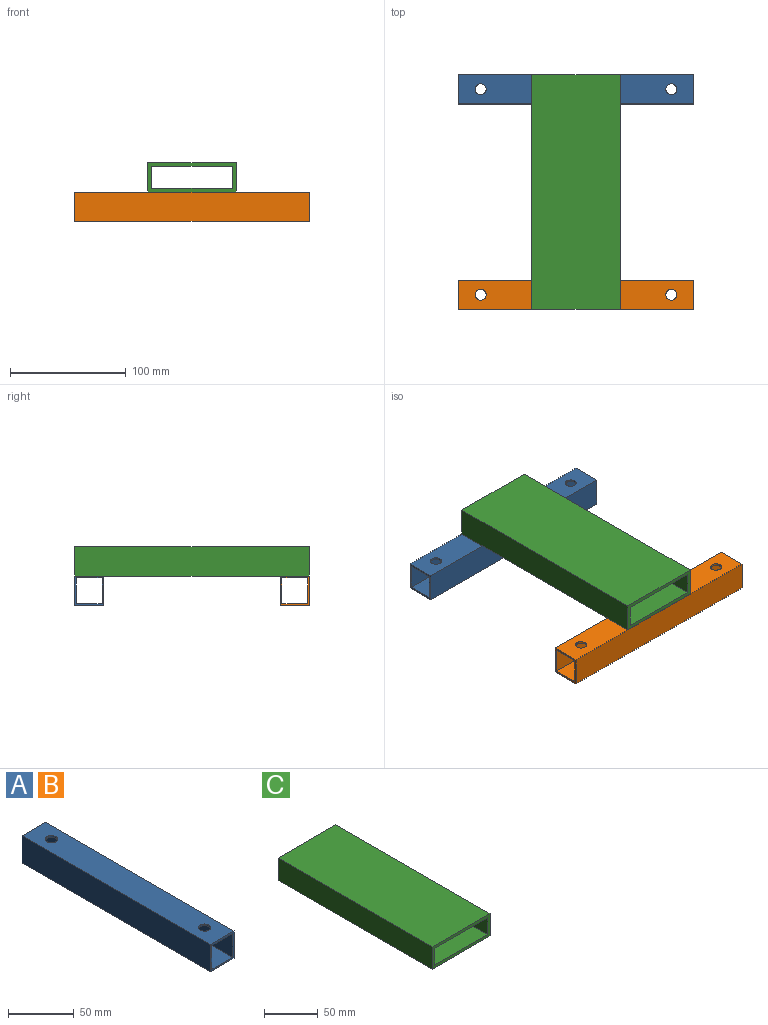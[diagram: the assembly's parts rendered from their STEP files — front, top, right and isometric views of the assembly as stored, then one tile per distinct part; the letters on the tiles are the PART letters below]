
ASSEMBLY  parts=3 mates=2
PART A: 14 faces, bbox 25.4x203.2x25.4 mm
  f0: plane 203.2x22.23mm, normal (1,0,0), area 4516.1mm2, adj f1,f7,f8,f9
  f1: plane 203.2x22.23mm, normal (0,0,-1), area 4373.6mm2, adj f0,f2,f8,f9,f12,f13
  f2: plane 203.2x22.23mm, normal (-1,0,0), area 4516.1mm2, adj f1,f7,f8,f9
  f3: plane 203.2x25.4mm, normal (1,0,0), area 5161.3mm2, adj f4,f6,f8,f9
  f4: plane 203.2x25.4mm, normal (0,0,1), area 5018.8mm2, adj f3,f5,f8,f9,f12,f13
  f5: plane 203.2x25.4mm, normal (-1,0,0), area 5161.3mm2, adj f4,f6,f8,f9
  f6: plane 203.2x25.4mm, normal (0,0,-1), area 5018.8mm2, adj f3,f5,f8,f9,f10,f11
  f7: plane 203.2x22.23mm, normal (0,0,1), area 4373.6mm2, adj f0,f2,f8,f9,f10,f11
  f8: plane 25.4x25.4mm, normal (0,-1,0), area 151.2mm2, adj f0,f1,f2,f3,f4,f5,f6,f7
  f9: plane 25.4x25.4mm, normal (0,1,0), area 151.2mm2, adj f0,f1,f2,f3,f4,f5,f6,f7
  f10: cylinder r=4.76mm len=9.53mm, axis (0,0,1), area 47.5mm2, adj f6,f7
  f11: cylinder r=4.76mm len=9.53mm, axis (0,0,1), area 47.5mm2, adj f6,f7
  f12: cylinder r=4.76mm len=9.53mm, axis (0,0,1), area 47.5mm2, adj f1,f4
  f13: cylinder r=4.76mm len=9.53mm, axis (0,0,1), area 47.5mm2, adj f1,f4
PART B: same geometry as A
PART C: 10 faces, bbox 76.2x203.2x25.4 mm
  f0: plane 203.2x19.05mm, normal (1,0,0), area 3871mm2, adj f1,f7,f8,f9
  f1: plane 203.2x69.85mm, normal (0,0,-1), area 14193.5mm2, adj f0,f2,f8,f9
  f2: plane 203.2x19.05mm, normal (-1,0,0), area 3871mm2, adj f1,f7,f8,f9
  f3: plane 203.2x25.4mm, normal (1,0,0), area 5161.3mm2, adj f4,f6,f8,f9
  f4: plane 203.2x76.2mm, normal (0,0,1), area 15483.8mm2, adj f3,f5,f8,f9
  f5: plane 203.2x25.4mm, normal (-1,0,0), area 5161.3mm2, adj f4,f6,f8,f9
  f6: plane 203.2x76.2mm, normal (0,0,-1), area 15483.8mm2, adj f3,f5,f8,f9
  f7: plane 203.2x69.85mm, normal (0,0,1), area 14193.5mm2, adj f0,f2,f8,f9
  f8: plane 76.2x25.4mm, normal (0,-1,0), area 604.8mm2, adj f0,f1,f2,f3,f4,f5,f6,f7
  f9: plane 76.2x25.4mm, normal (0,1,0), area 604.8mm2, adj f0,f1,f2,f3,f4,f5,f6,f7
PLACE A rot(axis=(0,0,1),90deg) t=(-21.41,76.36,-25.66)mm
PLACE B rot(axis=(0,0,1),90deg) t=(-21.41,-101.44,-25.66)mm
PLACE C t=(-21.41,-12.54,-0.26)mm
MATE fastened B.f4 <-> C.f6  axis (0,0,1) through (-21.41,-114.14,-12.96)mm
MATE fastened A.f4 <-> C.f6  axis (0,0,1) through (-21.41,89.06,-12.96)mm
